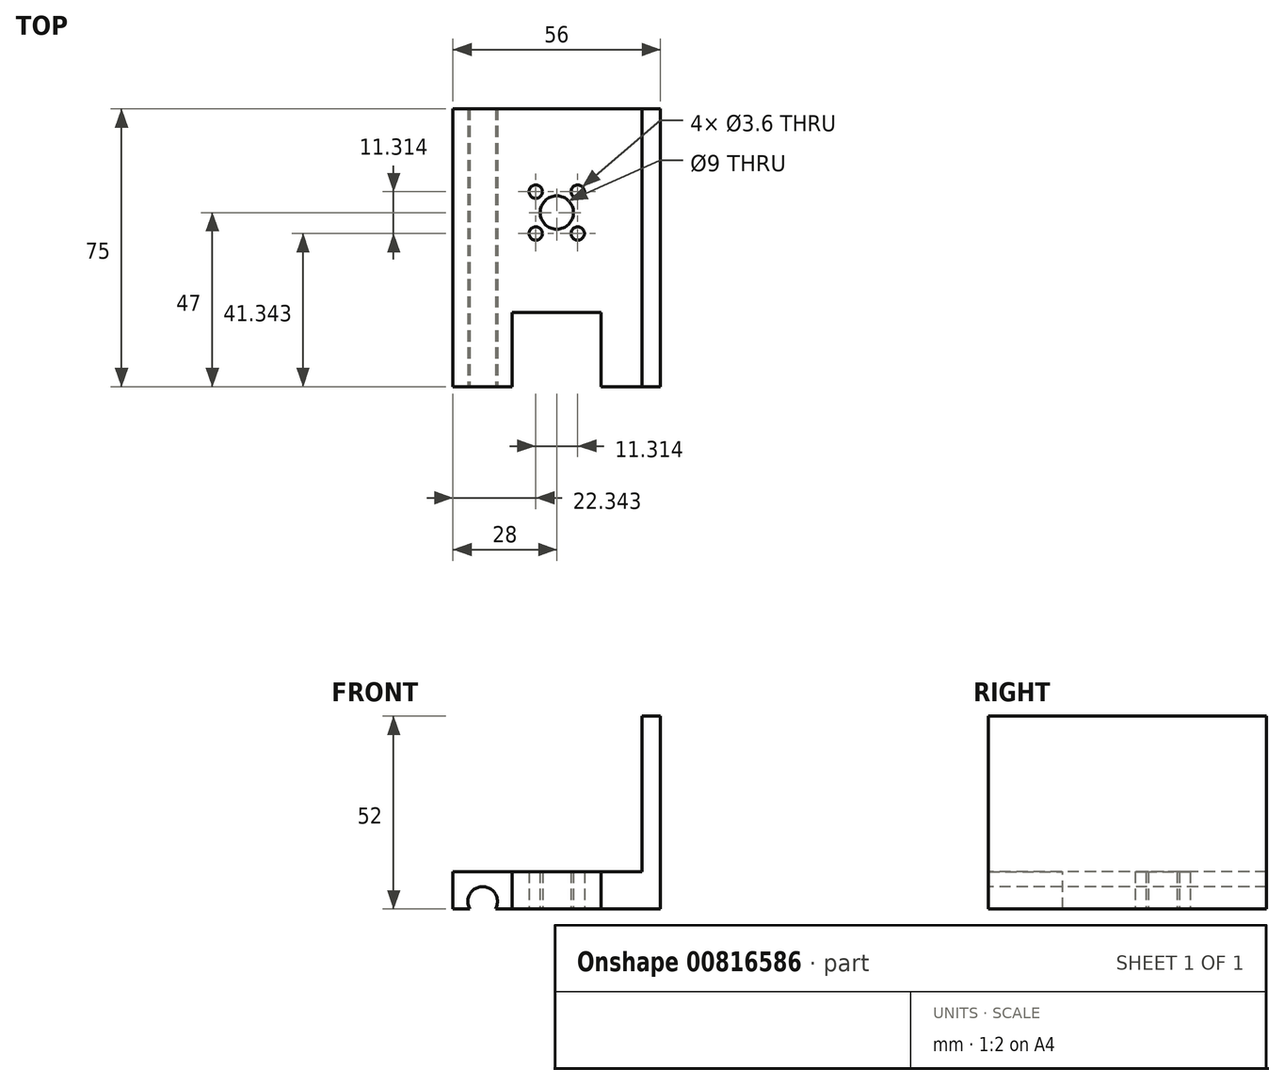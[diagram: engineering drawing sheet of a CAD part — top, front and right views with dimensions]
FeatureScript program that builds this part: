
annotation { "Feature Type Name" : "Feature", "Feature Type Description" : "" }
export const myFeature = defineFeature(function(context is Context, id is Id, definition is map)
    precondition{}
    {
        {
            var Q0;
            Q0=qCreatedBy(makeId("Top.planeOp"),FACE);
            var sketch = newSketch(context, id + "F0", { "sketchPlane" : qUnion([Q0])});
            skLineSegment(sketch, "E0.bottom", {"start": v(28, 37.5) * mm, "end": v(-28, 37.5) * mm});
            skLineSegment(sketch, "E0.left", {"start": v(28, 37.5) * mm, "end": v(28, -37.5) * mm});
            skLineSegment(sketch, "E0.right", {"start": v(-28, 37.5) * mm, "end": v(-28, -37.5) * mm});
            skLineSegment(sketch, "E1", {"start": v(-28, -37.5) * mm, "end": v(28, -37.5) * mm});
            skLineSegment(sketch, "E2", {"start": v(0, 37.5) * mm, "end": v(0, -37.5) * mm, "construction": true});
            skCircle(sketch, "E3", {"center": v(0, 9.5) * mm, "radius": 4.5 * mm});
            skCircle(sketch, "E4", {"center": v(0, 9.5) * mm, "radius": 8 * mm, "construction": true});
            skCircle(sketch, "E5", {"center": v(-5.66, 15.16) * mm, "radius": 1.8 * mm});
            skCircle(sketch, "E6.1.0", {"center": v(-5.66, 3.84) * mm, "radius": 1.8 * mm});
            skCircle(sketch, "E6.2.0", {"center": v(5.66, 3.84) * mm, "radius": 1.8 * mm});
            skCircle(sketch, "E6.3.0", {"center": v(5.66, 15.16) * mm, "radius": 1.8 * mm});
            skLineSegment(sketch, "E7", {"start": v(-5.66, 15.16) * mm, "end": v(-5.66, 3.84) * mm, "construction": true});
            skSolve(sketch);
        }
        {
            var Q0;
            Q0=makeQuery(id+"F0.imprint","IMPRINT",FACE,{"disambiguationData":[TD([[makeQuery(id+"F0.imprint","IMPRINT",EDGE,{"derivedFrom":sQuery(id+"F0.wireOp",EDGE,"E0.bottom")}),1.0]])]});
            extrude(context, id + "F1", {"entities" : qUnion([Q0]), "depth" : 10 * mm, "offsetDistance" : 25 * mm});
        }
        {
            var Q0;
            Q0=makeQuery(id+"F1.opExtrude","SWEPT_FACE",FACE,{"disambiguationData":[OSD([sQuery(id+"F0.wireOp",EDGE,"E1")])]});
            var sketch = newSketch(context, id + "F2", { "sketchPlane" : qUnion([Q0])});
            skLineSegment(sketch, "E8", {"start": v(-28, 2) * mm, "end": v(28, 2) * mm, "construction": true});
            skLineSegment(sketch, "E9", {"start": v(0, 10) * mm, "end": v(0, 0) * mm, "construction": true});
            skCircle(sketch, "E10", {"center": v(-20, 2) * mm, "radius": 4 * mm});
            skCircle(sketch, "E11.MirrorC", {"center": v(20, 2) * mm, "radius": 4 * mm});
            skSolve(sketch);
        }
        {
            var Q0;
            {var subQ0=sQuery(id+"F2.wireOp",EDGE,"E10");var subQ1=makeQuery(id+"F1.opExtrude","CAP_EDGE",EDGE,{"disambiguationData":[OSD([sQuery(id+"F0.wireOp",EDGE,"E1")])],"isStart":true});var subQ2=makeQuery(id+"F2.imprint","INTERSECT",VERTEX,{"disambiguationData":[OD(0.0)],"derivedFrom":[subQ1,subQ0]});Q0=makeQuery(id+"F2.imprint","IMPRINT",FACE,{"disambiguationData":[TD([[makeQuery(id+"F2.imprint","IMPRINT",EDGE,{"disambiguationData":[TD([[subQ2,1.0]])],"derivedFrom":subQ0}),1.0]])]});}
            var Q1;
            {var subQ0=sQuery(id+"F2.wireOp",EDGE,"E11.MirrorC");var subQ1=makeQuery(id+"F1.opExtrude","CAP_EDGE",EDGE,{"disambiguationData":[OSD([sQuery(id+"F0.wireOp",EDGE,"E1")])],"isStart":true});var subQ2=makeQuery(id+"F2.imprint","INTERSECT",VERTEX,{"disambiguationData":[OD(0.0)],"derivedFrom":[subQ1,subQ0]});Q1=makeQuery(id+"F2.imprint","IMPRINT",FACE,{"disambiguationData":[TD([[makeQuery(id+"F2.imprint","IMPRINT",EDGE,{"disambiguationData":[TD([[subQ2,1.0]])],"derivedFrom":subQ0}),-1.0]])]});}
            extrude(context, id + "F3", {"entities" : qUnion([Q0, Q1]), "operationType" : NewBodyOperationType.REMOVE, "endBound" : BoundingType.THROUGH_ALL, "oppositeDirection" : true, "depth" : 25 * mm, "offsetDistance" : 25 * mm});
        }
        {
            var Q0;
            Q0=makeQuery(id+"F1.opExtrude","CAP_FACE",FACE,{"disambiguationData":[OSD([sQuery(id+"F0.wireOp",EDGE,"E0.bottom"),sQuery(id+"F0.wireOp",EDGE,"E0.left"),sQuery(id+"F0.wireOp",EDGE,"E0.right"),sQuery(id+"F0.wireOp",EDGE,"E1")])],"isStart":false});
            var sketch = newSketch(context, id + "F4", { "sketchPlane" : qUnion([Q0])});
            skLineSegment(sketch, "E12.bottom", {"start": v(-12, -37.5) * mm, "end": v(12, -37.5) * mm});
            skLineSegment(sketch, "E12.top", {"start": v(-12, -17.5) * mm, "end": v(12, -17.5) * mm});
            skLineSegment(sketch, "E12.left", {"start": v(-12, -37.5) * mm, "end": v(-12, -17.5) * mm});
            skLineSegment(sketch, "E12.right", {"start": v(12, -37.5) * mm, "end": v(12, -17.5) * mm});
            skLineSegment(sketch, "E13", {"start": v(0, 37.5) * mm, "end": v(0, -37.5) * mm, "construction": true});
            skSolve(sketch);
        }
        {
            var Q0;
            Q0 = qSketchRegion(id + "F4", true);
            extrude(context, id + "F5", {"entities" : qUnion([Q0]), "operationType" : NewBodyOperationType.REMOVE, "oppositeDirection" : true, "depth" : 25 * mm, "offsetDistance" : 25 * mm});
        }
        {
            var Q0;
            Q0=makeQuery(id+"F1.opExtrude","CAP_FACE",FACE,{"disambiguationData":[OSD([sQuery(id+"F0.wireOp",EDGE,"E0.bottom"),sQuery(id+"F0.wireOp",EDGE,"E0.left"),sQuery(id+"F0.wireOp",EDGE,"E0.right"),sQuery(id+"F0.wireOp",EDGE,"E1"),sQuery(id+"F0.wireOp",EDGE,"E3"),sQuery(id+"F0.wireOp",EDGE,"E5"),sQuery(id+"F0.wireOp",EDGE,"E6.1.0"),sQuery(id+"F0.wireOp",EDGE,"E6.2.0"),sQuery(id+"F0.wireOp",EDGE,"E6.3.0")])],"isStart":false});
            var sketch = newSketch(context, id + "F6", { "sketchPlane" : qUnion([Q0])});
            skLineSegment(sketch, "E14.bottom", {"start": v(28, 37.5) * mm, "end": v(23, 37.5) * mm});
            skLineSegment(sketch, "E14.top", {"start": v(28, -37.5) * mm, "end": v(23, -37.5) * mm});
            skLineSegment(sketch, "E14.left", {"start": v(28, 37.5) * mm, "end": v(28, -37.5) * mm});
            skLineSegment(sketch, "E14.right", {"start": v(23, 37.5) * mm, "end": v(23, -37.5) * mm});
            skSolve(sketch);
        }
        {
            var Q0;
            Q0=makeQuery(id+"F6.imprint","IMPRINT",FACE,{"disambiguationData":[TD([[makeQuery(id+"F6.imprint","IMPRINT",EDGE,{"derivedFrom":sQuery(id+"F6.wireOp",EDGE,"E14.bottom")}),1.0]])]});
            extrude(context, id + "F7", {"entities" : qUnion([Q0]), "operationType" : NewBodyOperationType.ADD, "depth" : 42 * mm, "offsetDistance" : 25 * mm});
        }
    });
